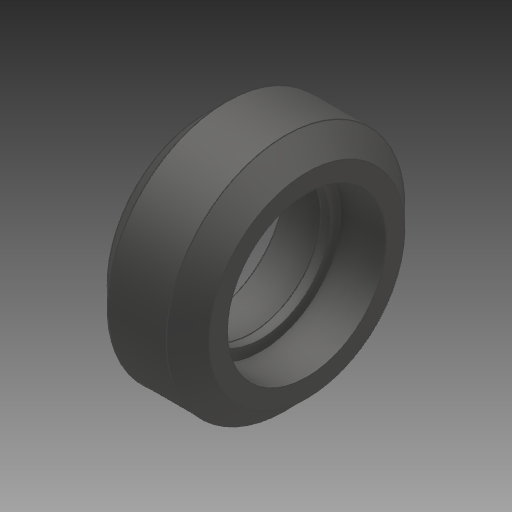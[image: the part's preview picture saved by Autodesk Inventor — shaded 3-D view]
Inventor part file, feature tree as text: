
AUTODESK INVENTOR PART (.ipt)
format: ipt  version: 2017 (Build 210142000, 142)  size: 140,288 bytes
history: mixed  units: mm
features: revolve x1, imported_body x1
ambient origin geometry x8: Origin, YZ Plane, XZ Plane, XY Plane, X Axis, Y Axis, Z Axis, Center Point
bodies: Solid1 (imported_parasolid)
feature tree (2):
  revolve  "Revolve1"  [1 undecoded]
  imported_body  NMx_Import_Brep_tag  [imported B-rep: ~10 faces, bbox_mm=[10.2, 0.0, 4.95]]
note: 1 required parameter value undecoded (feature->parameter linkage not recoverable at this tier; creation-order binding heuristic only, values carry confidence <= 0.55)
